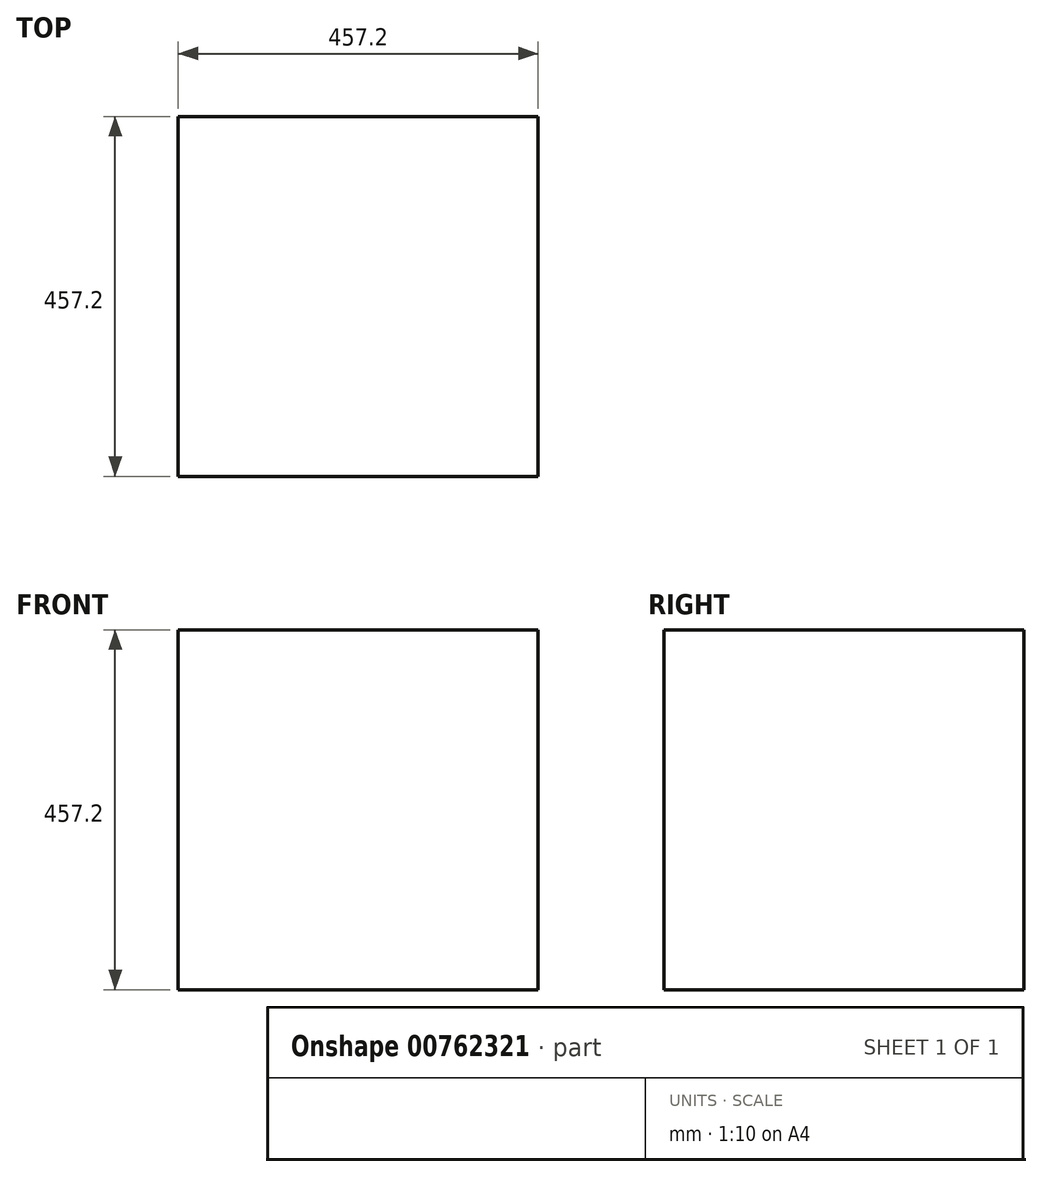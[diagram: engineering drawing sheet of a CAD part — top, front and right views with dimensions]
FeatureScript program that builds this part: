
annotation { "Feature Type Name" : "Feature", "Feature Type Description" : "" }
export const myFeature = defineFeature(function(context is Context, id is Id, definition is map)
    precondition{}
    {
        {
            var Q0;
            Q0=qCreatedBy(makeId("Front.planeOp"),FACE);
            var sketch = newSketch(context, id + "F0", { "sketchPlane" : qUnion([Q0])});
            skLineSegment(sketch, "E0.bottom", {"start": v(0, 11.19) * mm, "end": v(-457.2, 11.19) * mm});
            skLineSegment(sketch, "E0.top", {"start": v(0, 468.39) * mm, "end": v(-457.2, 468.39) * mm});
            skLineSegment(sketch, "E0.left", {"start": v(0, 11.19) * mm, "end": v(0, 468.39) * mm});
            skLineSegment(sketch, "E0.right", {"start": v(-457.2, 11.19) * mm, "end": v(-457.2, 468.39) * mm});
            skSolve(sketch);
        }
        {
            var Q0;
            Q0 = qSketchRegion(id + "F0", true);
            extrude(context, id + "F1", {"entities" : qUnion([Q0]), "depth" : 457.2 * mm, "offsetDistance" : 25.4 * mm});
        }
    });
